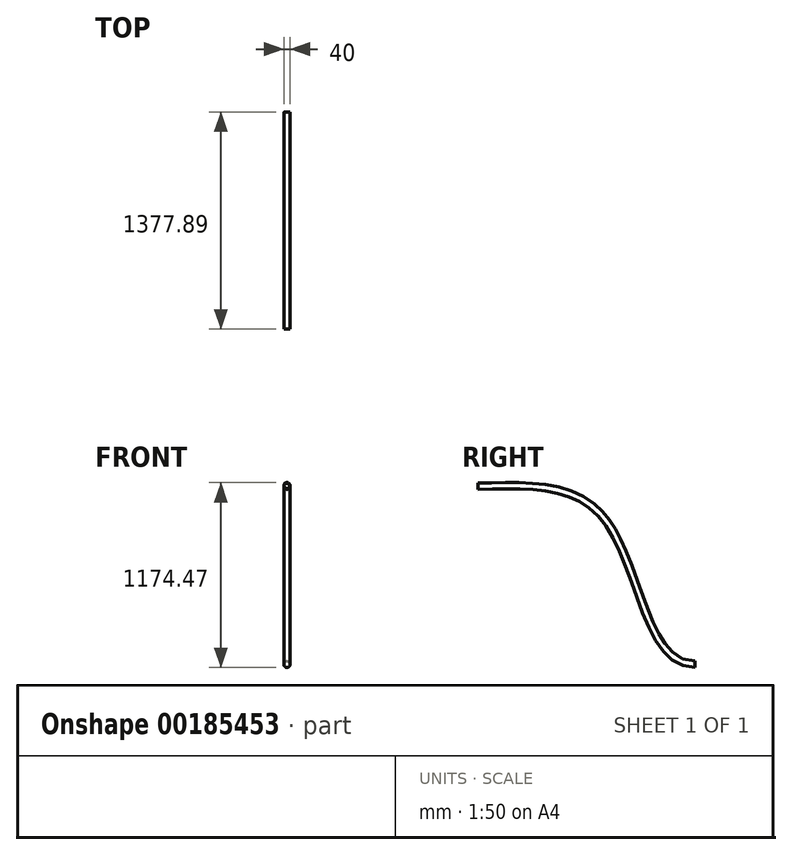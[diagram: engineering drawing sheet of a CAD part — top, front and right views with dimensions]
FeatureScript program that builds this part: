
annotation { "Feature Type Name" : "Feature", "Feature Type Description" : "" }
export const myFeature = defineFeature(function(context is Context, id is Id, definition is map)
    precondition{}
    {
        {
            var Q0;
            Q0=qCreatedBy(makeId("Right.planeOp"),FACE);
            var sketch = newSketch(context, id + "F0", { "sketchPlane" : qUnion([Q0])});
            skPoint(sketch, "E0", {"position": v(0, 0) * mm});
            skPoint(sketch, "E1", {"position": v(1377.81, 0) * mm});
            skPoint(sketch, "E2", {"position": v(1377.81, -1131.08) * mm});
            skSolve(sketch);
        }
        {
            var Q0;
            Q0=qCreatedBy(makeId("Right.planeOp"),FACE);
            var sketch = newSketch(context, id + "F1", { "sketchPlane" : qUnion([Q0])});
            skFitSpline(sketch, "E3", {"points": [v(0, 0) * mm, v(822.6, -230.88) * mm, v(1377.81, -1131.08) * mm], "startDerivative": vector(2109.81, 45.67) * mm, "endDerivative": vector(1760.39, 46.22) * mm});
            skSolve(sketch);
        }
        {
            var Q0;
            Q0=qCreatedBy(makeId("Front.planeOp"),FACE);
            var sketch = newSketch(context, id + "F2", { "sketchPlane" : qUnion([Q0])});
            skCircle(sketch, "E4", {"center": v(0, 2.52) * mm, "radius": 20 * mm});
            skCircle(sketch, "E5.0", {"center": v(0, 2.52) * mm, "radius": 18 * mm});
            skSolve(sketch);
        }
        {
            var Q0;
            Q0=makeQuery(id+"F2.imprint","IMPRINT",FACE,{"disambiguationData":[TD([[makeQuery(id+"F2.imprint","IMPRINT",EDGE,{"derivedFrom":sQuery(id+"F2.wireOp",EDGE,"E4")}),1.0]])]});
            var Q1;
            Q1=sQuery(id+"F1.wireOp",EDGE,"E3");
            sweep(context, id + "F3", {"profiles" : qUnion([Q0]), "path" : qUnion([Q1])});
        }
    });
